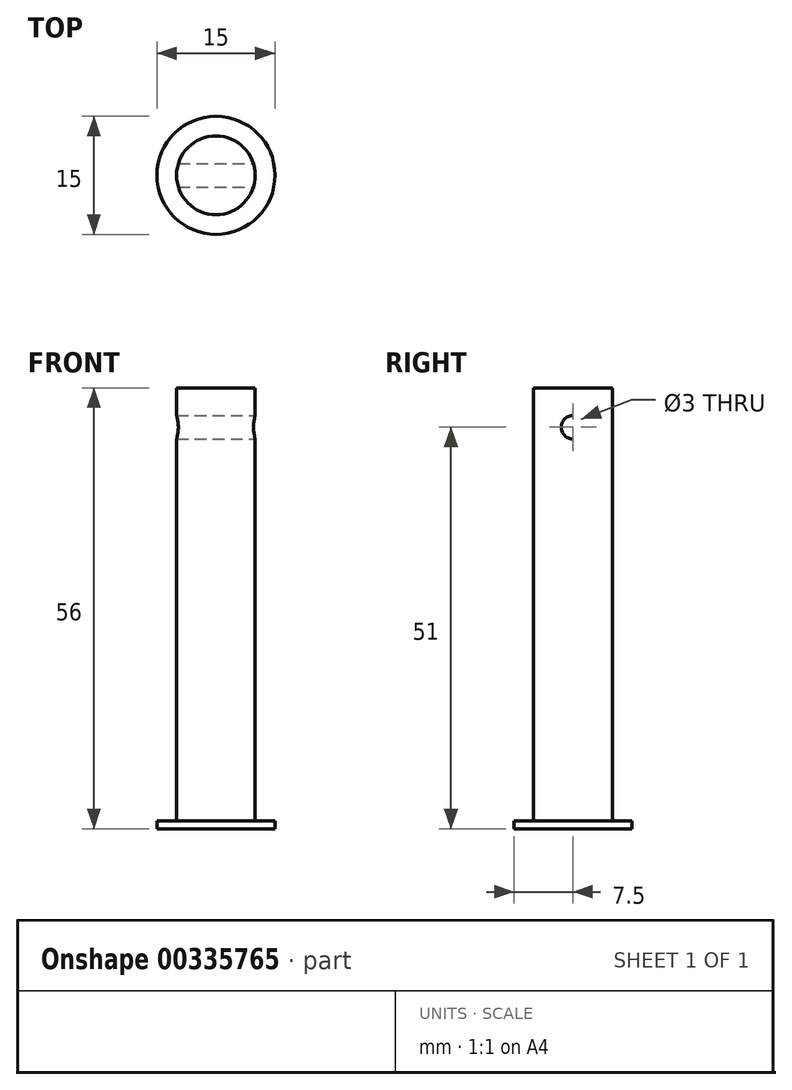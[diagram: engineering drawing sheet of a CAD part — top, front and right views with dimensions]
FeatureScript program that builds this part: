
annotation { "Feature Type Name" : "Feature", "Feature Type Description" : "" }
export const myFeature = defineFeature(function(context is Context, id is Id, definition is map)
    precondition{}
    {
        {
            var Q0;
            Q0=qCreatedBy(makeId("Top.planeOp"),FACE);
            var sketch = newSketch(context, id + "F0", { "sketchPlane" : qUnion([Q0])});
            skCircle(sketch, "E0", {"center": v(0, 0) * mm, "radius": 7.5 * mm});
            skSolve(sketch);
        }
        {
            var Q0;
            Q0 = qSketchRegion(id + "F0", true);
            extrude(context, id + "F1", {"entities" : qUnion([Q0]), "depth" : 1 * mm});
        }
        {
            var Q0;
            Q0=makeQuery(id+"F1.opExtrude","CAP_FACE",FACE,{"disambiguationData":[OSD([sQuery(id+"F0.wireOp",EDGE,"E0")])],"isStart":false});
            var sketch = newSketch(context, id + "F2", { "sketchPlane" : qUnion([Q0])});
            skCircle(sketch, "E1", {"center": v(0, 0) * mm, "radius": 5 * mm});
            skSolve(sketch);
        }
        {
            var Q0;
            Q0=makeQuery(id+"F2.imprint","IMPRINT",FACE,{"disambiguationData":[TD([[makeQuery(id+"F2.imprint","IMPRINT",EDGE,{"derivedFrom":sQuery(id+"F2.wireOp",EDGE,"E1")}),1.0]])]});
            extrude(context, id + "F3", {"entities" : qUnion([Q0]), "operationType" : NewBodyOperationType.ADD, "depth" : 55 * mm});
        }
        {
            var Q0;
            Q0 = qBodyType(qCreatedBy(id + "FlZheapfuu29z6b_1" ,EDGE), BodyType.WIRE);
            var Q1;
            Q1=qCreatedBy(makeId("Right.planeOp"),FACE);
            cPlane(context, id + "F4", {"entities" : qUnion([Q0, Q1]), "cplaneType" : CPlaneType.OFFSET, "offset" : 25 * mm, "width" : 150 * mm, "height" : 150 * mm});
        }
        {
            var Q0;
            Q0=qCreatedBy(id+"F4.planeOp",FACE);
            var sketch = newSketch(context, id + "F5", { "sketchPlane" : qUnion([Q0])});
            skCircle(sketch, "E2", {"center": v(0, 51) * mm, "radius": 1.5 * mm});
            skSolve(sketch);
        }
        {
            var Q0;
            Q0=makeQuery(id+"F5.imprint","IMPRINT",FACE,{"disambiguationData":[TD([[makeQuery(id+"F5.imprint","IMPRINT",EDGE,{"derivedFrom":sQuery(id+"F5.wireOp",EDGE,"E2")}),1.0]])]});
            extrude(context, id + "F6", {"entities" : qUnion([Q0]), "operationType" : NewBodyOperationType.REMOVE, "endBound" : BoundingType.THROUGH_ALL, "oppositeDirection" : true, "depth" : 25 * mm});
        }
        {
            var Q0;
            Q0 = qSketchRegion(id + "F2", true);
            extrude(context, id + "F7", {"entities" : qUnion([Q0]), "operationType" : NewBodyOperationType.ADD, "depth" : 48 * mm});
        }
    });
